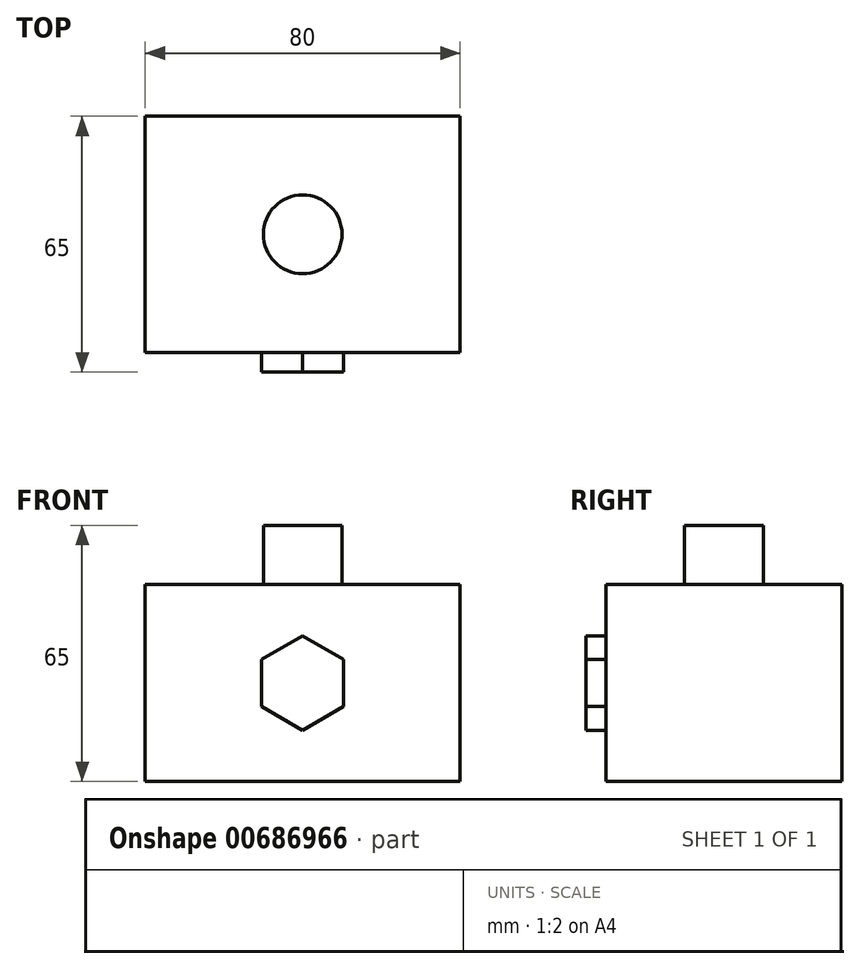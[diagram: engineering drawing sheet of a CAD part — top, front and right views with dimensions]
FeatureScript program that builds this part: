
annotation { "Feature Type Name" : "Feature", "Feature Type Description" : "" }
export const myFeature = defineFeature(function(context is Context, id is Id, definition is map)
    precondition{}
    {
        {
            var Q0;
            Q0=qCreatedBy(makeId("Top.planeOp"),FACE);
            var sketch = newSketch(context, id + "F0", { "sketchPlane" : qUnion([Q0])});
            skLineSegment(sketch, "E0.bottom", {"start": v(40, 30) * mm, "end": v(-40, 30) * mm});
            skLineSegment(sketch, "E0.top", {"start": v(40, -30) * mm, "end": v(-40, -30) * mm});
            skLineSegment(sketch, "E0.left", {"start": v(40, 30) * mm, "end": v(40, -30) * mm});
            skLineSegment(sketch, "E0.right", {"start": v(-40, 30) * mm, "end": v(-40, -30) * mm});
            skPoint(sketch, "E0.middle", {"position": v(0, 0) * mm});
            skSolve(sketch);
        }
        {
            var Q0;
            Q0 = qSketchRegion(id + "F0", true);
            extrude(context, id + "F1", {"entities" : qUnion([Q0]), "depth" : 50 * mm, "offsetDistance" : 25 * mm});
        }
        {
            var Q0;
            Q0=makeQuery(id+"F1.opExtrude","CAP_FACE",FACE,{"disambiguationData":[OSD([sQuery(id+"F0.wireOp",EDGE,"E0.bottom"),sQuery(id+"F0.wireOp",EDGE,"E0.top"),sQuery(id+"F0.wireOp",EDGE,"E0.left"),sQuery(id+"F0.wireOp",EDGE,"E0.right")])],"isStart":false});
            var sketch = newSketch(context, id + "F2", { "sketchPlane" : qUnion([Q0])});
            skCircle(sketch, "E1", {"center": v(0, 0) * mm, "radius": 10 * mm});
            skSolve(sketch);
        }
        {
            var Q0;
            Q0 = qSketchRegion(id + "F2", true);
            extrude(context, id + "F3", {"entities" : qUnion([Q0]), "operationType" : NewBodyOperationType.ADD, "depth" : 15 * mm, "offsetDistance" : 25 * mm});
        }
        {
            var Q0;
            Q0=makeQuery(id+"F1.opExtrude","SWEPT_FACE",FACE,{"disambiguationData":[OSD([sQuery(id+"F0.wireOp",EDGE,"E0.top")])]});
            var sketch = newSketch(context, id + "F4", { "sketchPlane" : qUnion([Q0])});
            skCircle(sketch, "E2.cCircle", {"center": v(0, 25) * mm, "radius": 10.4 * mm, "construction": true});
            skLineSegment(sketch, "E2.0", {"start": v(0, 13) * mm, "end": v(-10.4, 19) * mm});
            skLineSegment(sketch, "E2.1", {"start": v(-10.4, 19) * mm, "end": v(-10.4, 31) * mm});
            skLineSegment(sketch, "E2.2", {"start": v(-10.4, 31) * mm, "end": v(0, 37) * mm});
            skLineSegment(sketch, "E2.3", {"start": v(0, 37) * mm, "end": v(10.4, 31) * mm});
            skLineSegment(sketch, "E2.4", {"start": v(10.4, 31) * mm, "end": v(10.4, 19) * mm});
            skLineSegment(sketch, "E2.5", {"start": v(10.4, 19) * mm, "end": v(0, 13) * mm});
            skPoint(sketch, "E2.0.midPoint", {"position": v(-5.2, 16) * mm});
            skSolve(sketch);
        }
        {
            var Q0;
            Q0 = qSketchRegion(id + "F4", true);
            extrude(context, id + "F5", {"entities" : qUnion([Q0]), "operationType" : NewBodyOperationType.ADD, "depth" : 5 * mm, "offsetDistance" : 25 * mm});
        }
    });
